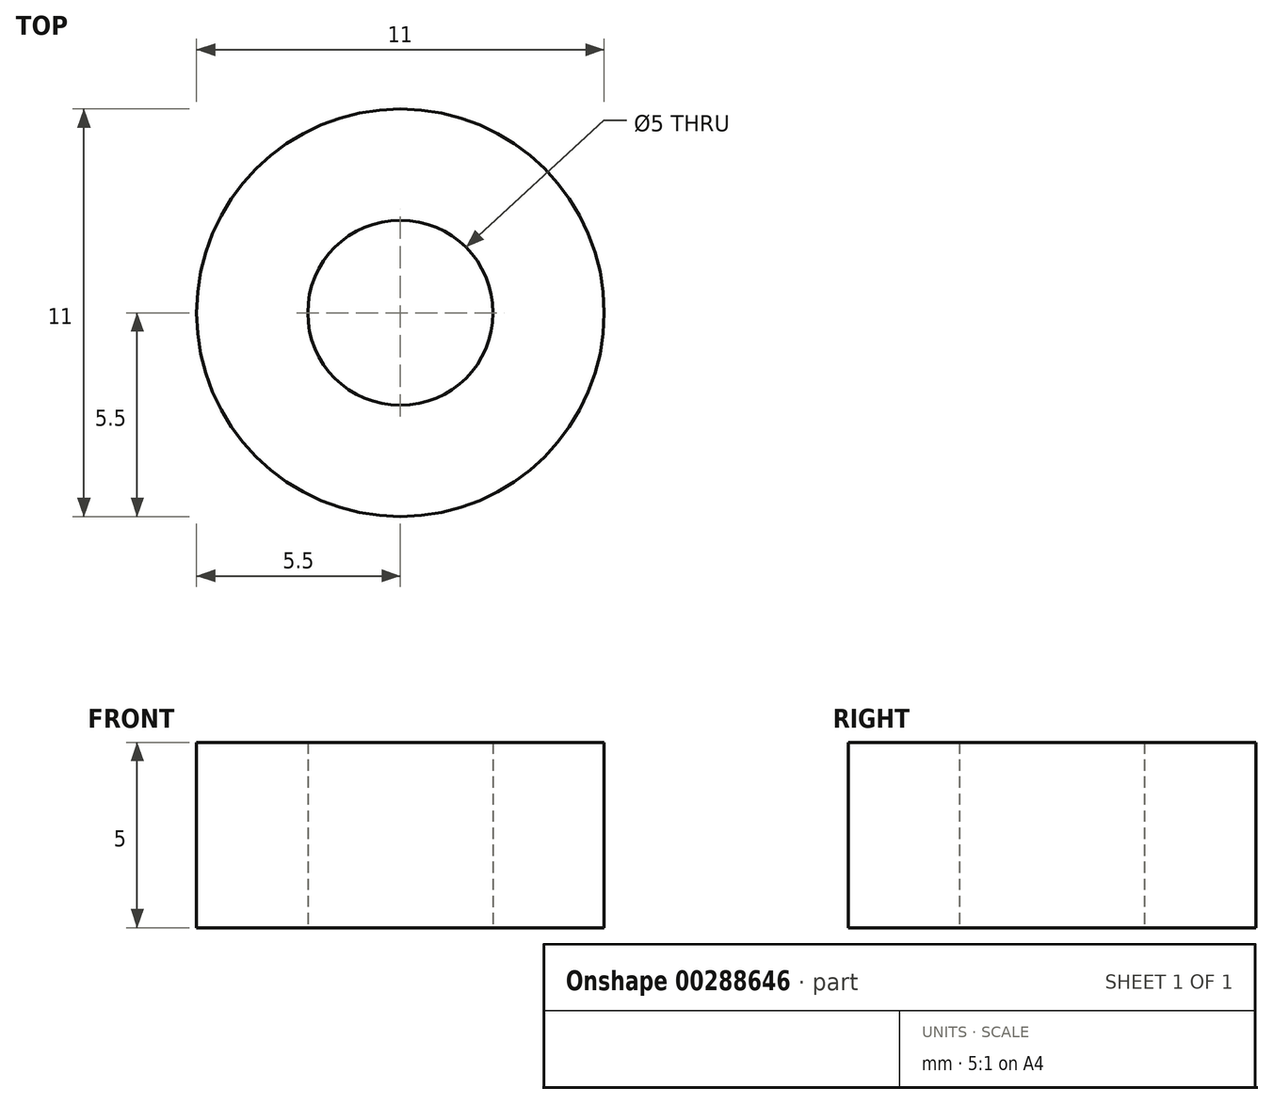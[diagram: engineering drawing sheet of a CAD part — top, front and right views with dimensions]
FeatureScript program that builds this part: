
annotation { "Feature Type Name" : "Feature", "Feature Type Description" : "" }
export const myFeature = defineFeature(function(context is Context, id is Id, definition is map)
    precondition{}
    {
        {
            var Q0;
            Q0=qCreatedBy(makeId("Top.planeOp"),FACE);
            var sketch = newSketch(context, id + "F0", { "sketchPlane" : qUnion([Q0])});
            skCircle(sketch, "E0", {"center": v(0, 0) * mm, "radius": 5.5 * mm});
            skCircle(sketch, "E1", {"center": v(0, 0) * mm, "radius": 2.5 * mm});
            skSolve(sketch);
        }
        {
            var Q0;
            Q0=makeQuery(id+"F0.imprint","IMPRINT",FACE,{"disambiguationData":[TD([[makeQuery(id+"F0.imprint","IMPRINT",EDGE,{"derivedFrom":sQuery(id+"F0.wireOp",EDGE,"E0")}),1.0]])]});
            extrude(context, id + "F1", {"entities" : qUnion([Q0]), "depth" : 5 * mm});
        }
    });
